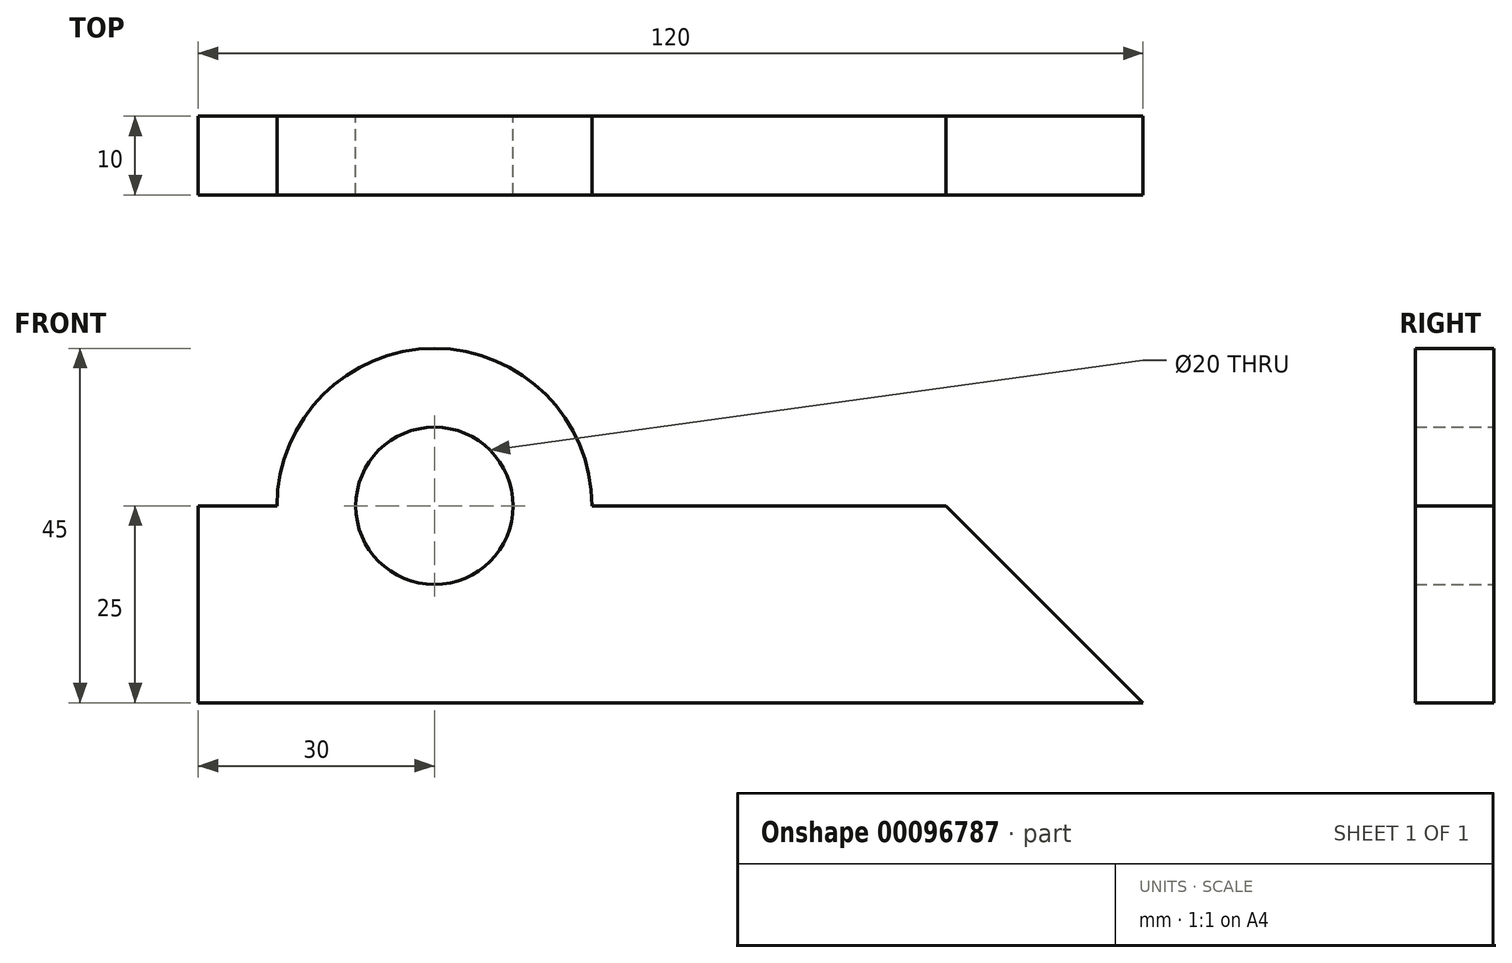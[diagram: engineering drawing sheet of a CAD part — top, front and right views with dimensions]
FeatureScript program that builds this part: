
annotation { "Feature Type Name" : "Feature", "Feature Type Description" : "" }
export const myFeature = defineFeature(function(context is Context, id is Id, definition is map)
    precondition{}
    {
        {
            var Q0;
            Q0=qCreatedBy(makeId("Front.planeOp"),FACE);
            var sketch = newSketch(context, id + "F0", { "sketchPlane" : qUnion([Q0])});
            skLineSegment(sketch, "E0", {"start": v(0, 0) * mm, "end": v(120, 0) * mm});
            skLineSegment(sketch, "E1", {"start": v(120, 0) * mm, "end": v(95, 25) * mm});
            skLineSegment(sketch, "E2", {"start": v(0, 0) * mm, "end": v(0, 25) * mm});
            skLineSegment(sketch, "E3", {"start": v(95, 25) * mm, "end": v(50, 25) * mm});
            skLineSegment(sketch, "E4", {"start": v(0, 25) * mm, "end": v(10, 25) * mm});
            skLineSegment(sketch, "E5", {"start": v(30, 45) * mm, "end": v(30, 0) * mm, "construction": true});
            skLineSegment(sketch, "E6", {"start": v(10, 25) * mm, "end": v(50, 25) * mm, "construction": true});
            skCircle(sketch, "E7", {"center": v(30, 25) * mm, "radius": 10 * mm});
            skArc(sketch, "E8", {"start": v(10, 25) * mm, "mid": v(30, 45) * mm, "end": v(50, 25) * mm});
            skSolve(sketch);
        }
        {
            var Q0;
            Q0 = qSketchRegion(id + "F0", true);
            extrude(context, id + "F1", {"entities" : qUnion([Q0]), "depth" : 10 * mm});
        }
    });
